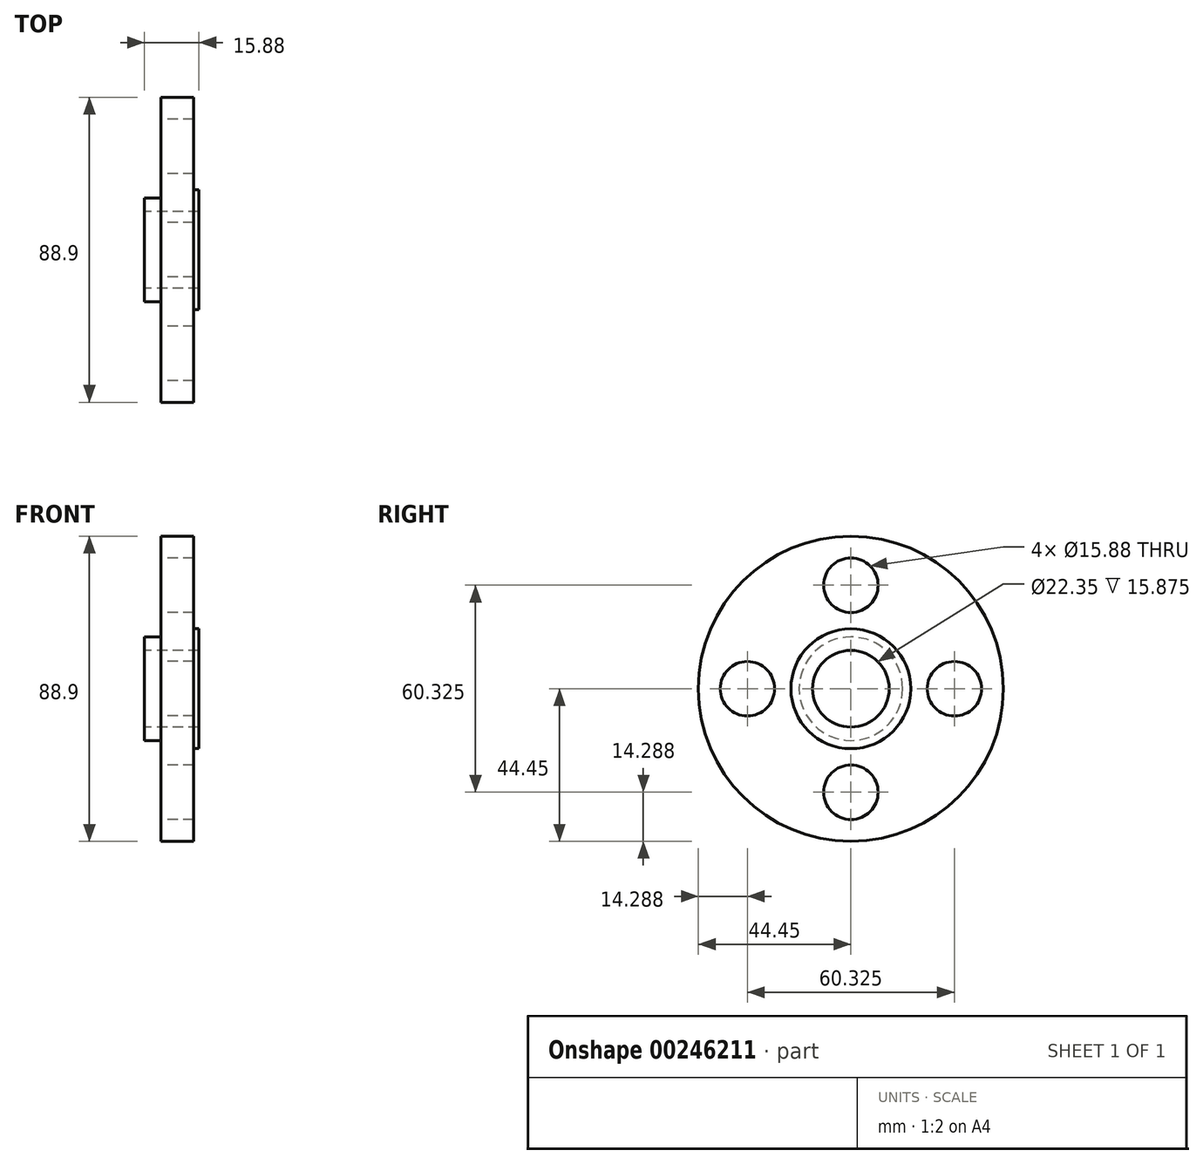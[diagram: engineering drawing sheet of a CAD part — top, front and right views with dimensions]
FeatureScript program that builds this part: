
annotation { "Feature Type Name" : "Feature", "Feature Type Description" : "" }
export const myFeature = defineFeature(function(context is Context, id is Id, definition is map)
    precondition{}
    {
        {
            var Q0;
            Q0=qCreatedBy(makeId("Front.planeOp"),FACE);
            var sketch = newSketch(context, id + "F0", { "sketchPlane" : qUnion([Q0])});
            skLineSegment(sketch, "E0", {"start": v(-37.13, 0) * mm, "end": v(50.6, 0) * mm, "construction": true});
            skLineSegment(sketch, "E1", {"start": v(0, 11.18) * mm, "end": v(15.88, 11.18) * mm});
            skLineSegment(sketch, "E2", {"start": v(15.88, 11.18) * mm, "end": v(15.88, 17.46) * mm});
            skLineSegment(sketch, "E3", {"start": v(15.88, 17.46) * mm, "end": v(14.35, 17.46) * mm});
            skLineSegment(sketch, "E4", {"start": v(14.35, 17.46) * mm, "end": v(14.35, 44.45) * mm});
            skLineSegment(sketch, "E5", {"start": v(14.35, 44.45) * mm, "end": v(4.78, 44.45) * mm});
            skLineSegment(sketch, "E6", {"start": v(4.78, 44.45) * mm, "end": v(4.78, 15.09) * mm});
            skLineSegment(sketch, "E7", {"start": v(4.78, 15.09) * mm, "end": v(0, 15.09) * mm});
            skLineSegment(sketch, "E8", {"start": v(0, 15.09) * mm, "end": v(0, 11.18) * mm});
            skSolve(sketch);
        }
        {
            var Q0;
            Q0=makeQuery(id+"F0.imprint","IMPRINT",FACE,{"disambiguationData":[TD([[makeQuery(id+"F0.imprint","IMPRINT",EDGE,{"derivedFrom":sQuery(id+"F0.wireOp",EDGE,"E1")}),1.0]])]});
            var Q1;
            Q1=sQuery(id+"F0.wireOp",EDGE,"E0");
            revolve(context, id + "F1", {"entities" : qUnion([Q0]), "axis" : qUnion([Q1]), "revolveType" : RevolveType.FULL});
        }
        {
            var Q0;
            Q0=qCreatedBy(makeId("Right.planeOp"),FACE);
            var sketch = newSketch(context, id + "F2", { "sketchPlane" : qUnion([Q0])});
            skCircle(sketch, "E9", {"center": v(0, 0) * mm, "radius": 30.16 * mm, "construction": true});
            skCircle(sketch, "E10", {"center": v(0, 30.16) * mm, "radius": 7.94 * mm});
            skCircle(sketch, "E11.1.0", {"center": v(-30.16, 0) * mm, "radius": 7.94 * mm});
            skCircle(sketch, "E11.2.0", {"center": v(0, -30.16) * mm, "radius": 7.94 * mm});
            skCircle(sketch, "E11.3.0", {"center": v(30.16, 0) * mm, "radius": 7.94 * mm});
            skSolve(sketch);
        }
        {
            var Q0;
            Q0 = qSketchRegion(id + "F2", true);
            extrude(context, id + "F3", {"entities" : qUnion([Q0]), "operationType" : NewBodyOperationType.REMOVE, "endBound" : BoundingType.THROUGH_ALL, "depth" : 25.4 * mm});
        }
    });
